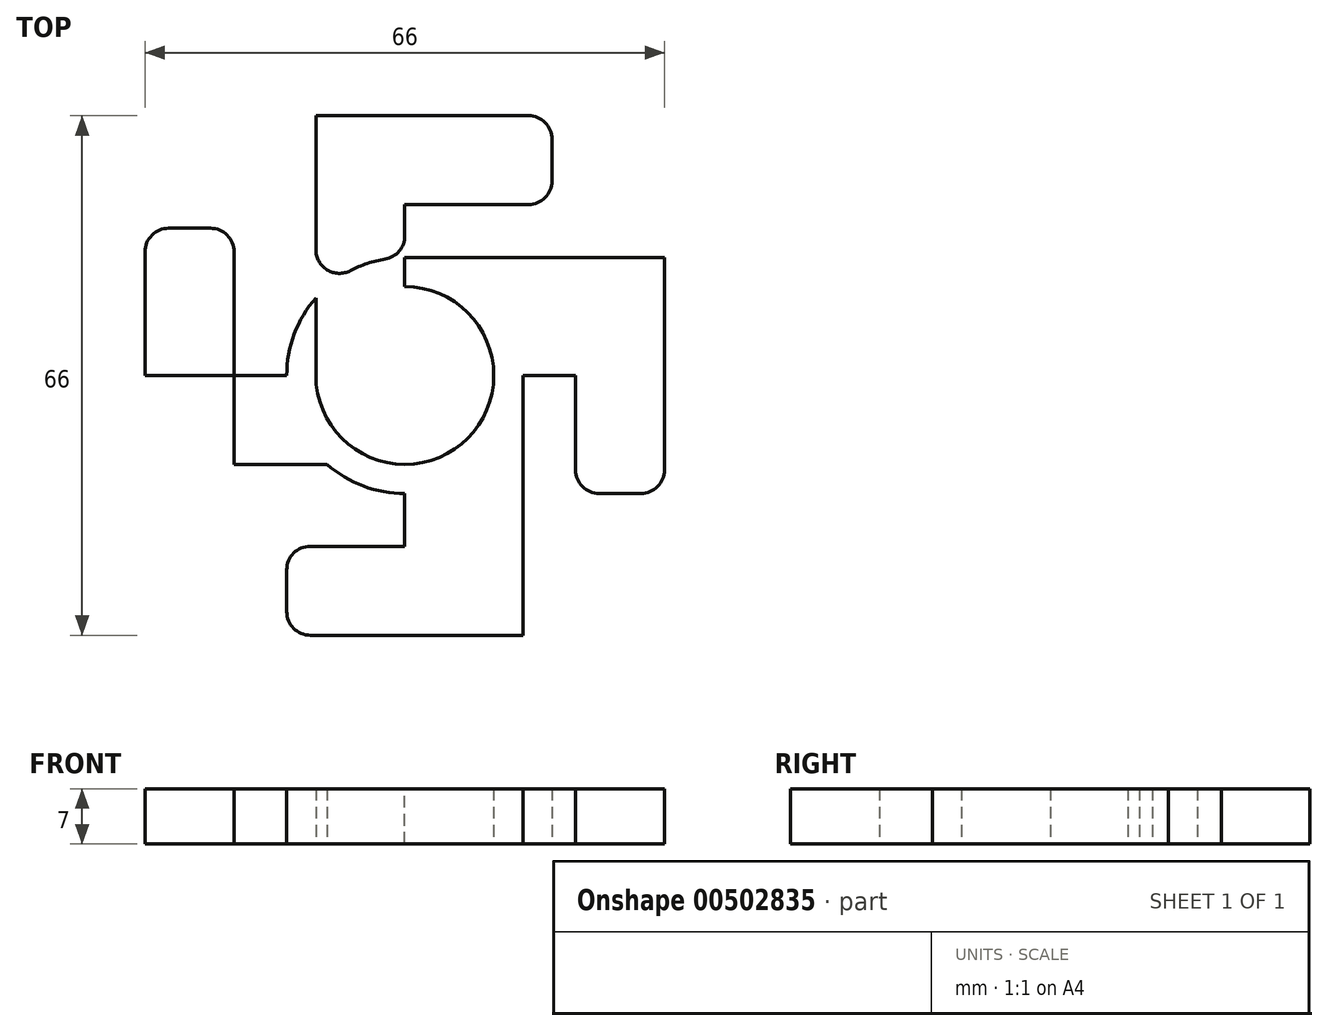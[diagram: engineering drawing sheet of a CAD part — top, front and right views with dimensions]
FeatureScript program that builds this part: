
annotation { "Feature Type Name" : "Feature", "Feature Type Description" : "" }
export const myFeature = defineFeature(function(context is Context, id is Id, definition is map)
    precondition{}
    {
        {
            var Q0;
            Q0=qCreatedBy(makeId("Top.planeOp"),FACE);
            var sketch = newSketch(context, id + "F0", { "sketchPlane" : qUnion([Q0])});
            skCircle(sketch, "E0", {"center": v(0, 0) * mm, "radius": 11.3 * mm});
            skLineSegment(sketch, "E1.bottom", {"start": v(0, 0) * mm, "end": v(33, 0) * mm});
            skLineSegment(sketch, "E1.top", {"start": v(0, 15) * mm, "end": v(33, 15) * mm});
            skLineSegment(sketch, "E1.left", {"start": v(0, 0) * mm, "end": v(0, 15) * mm});
            skLineSegment(sketch, "E1.right", {"start": v(33, 0) * mm, "end": v(33, 15) * mm});
            skLineSegment(sketch, "E2.bottom", {"start": v(33, 15) * mm, "end": v(21.7, 15) * mm});
            skLineSegment(sketch, "E2.top", {"start": v(33, -15) * mm, "end": v(21.7, -15) * mm});
            skLineSegment(sketch, "E2.left", {"start": v(33, 15) * mm, "end": v(33, -15) * mm});
            skLineSegment(sketch, "E2.right", {"start": v(21.7, 15) * mm, "end": v(21.7, -15) * mm});
            skLineSegment(sketch, "E3.bottom", {"start": v(0, 0) * mm, "end": v(15, 0) * mm});
            skLineSegment(sketch, "E3.top", {"start": v(0, -33) * mm, "end": v(15, -33) * mm});
            skLineSegment(sketch, "E3.left", {"start": v(0, 0) * mm, "end": v(0, -33) * mm});
            skLineSegment(sketch, "E3.right", {"start": v(15, 0) * mm, "end": v(15, -33) * mm});
            skLineSegment(sketch, "E4.bottom", {"start": v(15, -33) * mm, "end": v(-15, -33) * mm});
            skLineSegment(sketch, "E4.top", {"start": v(15, -21.7) * mm, "end": v(-15, -21.7) * mm});
            skLineSegment(sketch, "E4.left", {"start": v(15, -33) * mm, "end": v(15, -21.7) * mm});
            skLineSegment(sketch, "E4.right", {"start": v(-15, -33) * mm, "end": v(-15, -21.7) * mm});
            skLineSegment(sketch, "E5.bottom", {"start": v(0, 0) * mm, "end": v(-33, 0) * mm});
            skLineSegment(sketch, "E5.top", {"start": v(0, -11.3) * mm, "end": v(-33, -11.3) * mm});
            skLineSegment(sketch, "E5.left", {"start": v(0, 0) * mm, "end": v(0, -11.3) * mm});
            skLineSegment(sketch, "E5.right", {"start": v(-33, 0) * mm, "end": v(-33, -11.3) * mm});
            skLineSegment(sketch, "E6.bottom", {"start": v(-33, -11.3) * mm, "end": v(-21.7, -11.3) * mm});
            skLineSegment(sketch, "E6.top", {"start": v(-33, 18.7) * mm, "end": v(-21.7, 18.7) * mm});
            skLineSegment(sketch, "E6.left", {"start": v(-33, -11.3) * mm, "end": v(-33, 18.7) * mm});
            skLineSegment(sketch, "E6.right", {"start": v(-21.7, -11.3) * mm, "end": v(-21.7, 18.7) * mm});
            skLineSegment(sketch, "E7.bottom", {"start": v(0, 0) * mm, "end": v(-11.3, 0) * mm});
            skLineSegment(sketch, "E7.top", {"start": v(0, 33) * mm, "end": v(-11.3, 33) * mm});
            skLineSegment(sketch, "E7.left", {"start": v(0, 0) * mm, "end": v(0, 33) * mm});
            skLineSegment(sketch, "E7.right", {"start": v(-11.3, 0) * mm, "end": v(-11.3, 33) * mm});
            skLineSegment(sketch, "E8.bottom", {"start": v(-11.3, 33) * mm, "end": v(18.7, 33) * mm});
            skLineSegment(sketch, "E8.top", {"start": v(-11.3, 21.7) * mm, "end": v(18.7, 21.7) * mm});
            skLineSegment(sketch, "E8.left", {"start": v(-11.3, 33) * mm, "end": v(-11.3, 21.7) * mm});
            skLineSegment(sketch, "E8.right", {"start": v(18.7, 33) * mm, "end": v(18.7, 21.7) * mm});
            skCircle(sketch, "E9", {"center": v(0, 0) * mm, "radius": 15 * mm});
            skSolve(sketch);
        }
        {
            var Q0;
            {var subQ1=sQuery(id+"F0.wireOp",EDGE,"E0");var subQ3=sQuery(id+"F0.wireOp",EDGE,"E7.left");var subQ4=makeQuery(id+"F0.imprint","INTERSECT",VERTEX,{"derivedFrom":[subQ1,subQ3]});Q0=makeQuery(id+"F0.imprint","IMPRINT",FACE,{"disambiguationData":[TD([[makeQuery(id+"F0.imprint","IMPRINT",EDGE,{"disambiguationData":[TD([[subQ4,-1.0]])],"derivedFrom":subQ3}),1.0]])]});}
            var Q1;
            {var subQ1=sQuery(id+"F0.wireOp",EDGE,"E5.bottom");var subQ3=sQuery(id+"F0.wireOp",EDGE,"E9");var subQ4=makeQuery(id+"F0.imprint","INTERSECT",VERTEX,{"derivedFrom":[subQ1,subQ3]});Q1=makeQuery(id+"F0.imprint","IMPRINT",FACE,{"disambiguationData":[TD([[makeQuery(id+"F0.imprint","IMPRINT",EDGE,{"disambiguationData":[TD([[subQ4,1.0]])],"derivedFrom":subQ3}),1.0]])]});}
            var Q2;
            {var subQ3=sQuery(id+"F0.wireOp",EDGE,"E5.bottom");var subQ5=sQuery(id+"F0.wireOp",EDGE,"E9");var subQ6=makeQuery(id+"F0.imprint","INTERSECT",VERTEX,{"derivedFrom":[subQ3,subQ5]});Q2=makeQuery(id+"F0.imprint","IMPRINT",FACE,{"disambiguationData":[TD([[makeQuery(id+"F0.imprint","IMPRINT",EDGE,{"disambiguationData":[TD([[subQ6,-1.0]])],"derivedFrom":subQ5}),1.0]])]});}
            var Q3;
            {var subQ0=sQuery(id+"F0.wireOp",EDGE,"E9");var subQ1=sQuery(id+"F0.wireOp",EDGE,"E5.bottom");var subQ2=makeQuery(id+"F0.imprint","INTERSECT",VERTEX,{"derivedFrom":[subQ1,subQ0]});Q3=makeQuery(id+"F0.imprint","IMPRINT",FACE,{"disambiguationData":[TD([[makeQuery(id+"F0.imprint","IMPRINT",EDGE,{"disambiguationData":[TD([[subQ2,-1.0]])],"derivedFrom":subQ1}),1.0]])]});}
            var Q4;
            {var subQ5=sQuery(id+"F0.wireOp",EDGE,"E6.bottom");Q4=makeQuery(id+"F0.imprint","IMPRINT",FACE,{"disambiguationData":[TD([[makeQuery(id+"F0.imprint","IMPRINT",EDGE,{"derivedFrom":subQ5}),1.0]])]});}
            var Q5;
            {var subQ5=sQuery(id+"F0.wireOp",EDGE,"E6.top");Q5=makeQuery(id+"F0.imprint","IMPRINT",FACE,{"disambiguationData":[TD([[makeQuery(id+"F0.imprint","IMPRINT",EDGE,{"derivedFrom":subQ5}),-1.0]])]});}
            var Q6;
            {var subQ1=sQuery(id+"F0.wireOp",EDGE,"E7.left");var subQ3=sQuery(id+"F0.wireOp",EDGE,"E8.top");var subQ4=makeQuery(id+"F0.imprint","INTERSECT",VERTEX,{"derivedFrom":[subQ1,subQ3]});Q6=makeQuery(id+"F0.imprint","IMPRINT",FACE,{"disambiguationData":[TD([[makeQuery(id+"F0.imprint","IMPRINT",EDGE,{"disambiguationData":[TD([[subQ4,1.0]])],"derivedFrom":subQ1}),1.0]])]});}
            var Q7;
            {var subQ5=sQuery(id+"F0.wireOp",EDGE,"E8.left");Q7=makeQuery(id+"F0.imprint","IMPRINT",FACE,{"disambiguationData":[TD([[makeQuery(id+"F0.imprint","IMPRINT",EDGE,{"derivedFrom":subQ5}),1.0]])]});}
            var Q8;
            {var subQ5=sQuery(id+"F0.wireOp",EDGE,"E8.right");Q8=makeQuery(id+"F0.imprint","IMPRINT",FACE,{"disambiguationData":[TD([[makeQuery(id+"F0.imprint","IMPRINT",EDGE,{"derivedFrom":subQ5}),-1.0]])]});}
            var Q9;
            {var subQ5=sQuery(id+"F0.wireOp",EDGE,"E1.top");Q9=makeQuery(id+"F0.imprint","IMPRINT",FACE,{"disambiguationData":[TD([[makeQuery(id+"F0.imprint","IMPRINT",EDGE,{"derivedFrom":subQ5}),-1.0]])]});}
            var Q10;
            {var subQ5=sQuery(id+"F0.wireOp",EDGE,"E2.bottom");Q10=makeQuery(id+"F0.imprint","IMPRINT",FACE,{"disambiguationData":[TD([[makeQuery(id+"F0.imprint","IMPRINT",EDGE,{"derivedFrom":subQ5}),1.0]])]});}
            var Q11;
            {var subQ5=sQuery(id+"F0.wireOp",EDGE,"E2.top");Q11=makeQuery(id+"F0.imprint","IMPRINT",FACE,{"disambiguationData":[TD([[makeQuery(id+"F0.imprint","IMPRINT",EDGE,{"derivedFrom":subQ5}),-1.0]])]});}
            var Q12;
            {var subQ5=sQuery(id+"F0.wireOp",EDGE,"E3.right");Q12=makeQuery(id+"F0.imprint","IMPRINT",FACE,{"disambiguationData":[TD([[makeQuery(id+"F0.imprint","IMPRINT",EDGE,{"derivedFrom":subQ5}),-1.0]])]});}
            var Q13;
            {var subQ5=sQuery(id+"F0.wireOp",EDGE,"E4.left");Q13=makeQuery(id+"F0.imprint","IMPRINT",FACE,{"disambiguationData":[TD([[makeQuery(id+"F0.imprint","IMPRINT",EDGE,{"derivedFrom":subQ5}),1.0]])]});}
            var Q14;
            {var subQ5=sQuery(id+"F0.wireOp",EDGE,"E4.right");Q14=makeQuery(id+"F0.imprint","IMPRINT",FACE,{"disambiguationData":[TD([[makeQuery(id+"F0.imprint","IMPRINT",EDGE,{"derivedFrom":subQ5}),-1.0]])]});}
            var Q15;
            {var subQ1=sQuery(id+"F0.wireOp",EDGE,"E0");var subQ3=sQuery(id+"F0.wireOp",EDGE,"E3.bottom");var subQ4=makeQuery(id+"F0.imprint","INTERSECT",VERTEX,{"derivedFrom":[subQ1,subQ3]});Q15=makeQuery(id+"F0.imprint","IMPRINT",FACE,{"disambiguationData":[TD([[makeQuery(id+"F0.imprint","IMPRINT",EDGE,{"disambiguationData":[TD([[subQ4,1.0]])],"derivedFrom":subQ1}),-1.0]])]});}
            var Q16;
            {var subQ1=sQuery(id+"F0.wireOp",EDGE,"E3.left");var subQ3=sQuery(id+"F0.wireOp",EDGE,"E9");var subQ4=makeQuery(id+"F0.imprint","INTERSECT",VERTEX,{"derivedFrom":[subQ1,subQ3]});Q16=makeQuery(id+"F0.imprint","IMPRINT",FACE,{"disambiguationData":[TD([[makeQuery(id+"F0.imprint","IMPRINT",EDGE,{"disambiguationData":[TD([[subQ4,1.0]])],"derivedFrom":subQ3}),1.0]])]});}
            var Q17;
            {var subQ0=sQuery(id+"F0.wireOp",EDGE,"E7.left");var subQ1=sQuery(id+"F0.wireOp",EDGE,"E0");var subQ2=makeQuery(id+"F0.imprint","INTERSECT",VERTEX,{"derivedFrom":[subQ1,subQ0]});Q17=makeQuery(id+"F0.imprint","IMPRINT",FACE,{"disambiguationData":[TD([[makeQuery(id+"F0.imprint","IMPRINT",EDGE,{"disambiguationData":[TD([[subQ2,1.0]])],"derivedFrom":subQ1}),-1.0]])]});}
            extrude(context, id + "F1", {"entities" : qUnion([Q0, Q1, Q2, Q3, Q4, Q5, Q6, Q7, Q8, Q9, Q10, Q11, Q12, Q13, Q14, Q15, Q16, Q17]), "depth" : 7 * mm});
        }
        {
            var Q0;
            Q0=makeQuery(id+"F1.opExtrude","SWEPT_EDGE",EDGE,{"disambiguationData":[OSD([sQuery(id+"F0.wireOp",EDGE,"E1.bottom"),sQuery(id+"F0.wireOp",EDGE,"E2.right")])]});
            var Q1;
            Q1=makeQuery(id+"F1.opExtrude","SWEPT_EDGE",EDGE,{"disambiguationData":[OSD([sQuery(id+"F0.wireOp",EDGE,"E3.left"),sQuery(id+"F0.wireOp",EDGE,"E4.top")])]});
            var Q2;
            Q2=makeQuery(id+"F1.opExtrude","SWEPT_EDGE",EDGE,{"disambiguationData":[OSD([sQuery(id+"F0.wireOp",EDGE,"E5.bottom"),sQuery(id+"F0.wireOp",EDGE,"E9")])]});
            var Q3;
            Q3=makeQuery(id+"F1.opExtrude","SWEPT_EDGE",EDGE,{"disambiguationData":[OSD([sQuery(id+"F0.wireOp",EDGE,"E1.top"),sQuery(id+"F0.wireOp",EDGE,"E7.left"),sQuery(id+"F0.wireOp",EDGE,"E9")])]});
            var Q4;
            Q4=makeQuery(id+"F1.opExtrude","SWEPT_EDGE",EDGE,{"disambiguationData":[OSD([sQuery(id+"F0.wireOp",EDGE,"E7.right"),sQuery(id+"F0.wireOp",EDGE,"E9")])]});
            var Q5;
            Q5=makeQuery(id+"F1.opExtrude","SWEPT_EDGE",EDGE,{"disambiguationData":[OSD([sQuery(id+"F0.wireOp",EDGE,"E3.left"),sQuery(id+"F0.wireOp",EDGE,"E9")])]});
            var Q6;
            Q6=makeQuery(id+"F1.opExtrude","SWEPT_EDGE",EDGE,{"disambiguationData":[OSD([sQuery(id+"F0.wireOp",EDGE,"E5.top"),sQuery(id+"F0.wireOp",EDGE,"E9")])]});
            var Q7;
            Q7=makeQuery(id+"F1.opExtrude","SWEPT_EDGE",EDGE,{"disambiguationData":[OSD([sQuery(id+"F0.wireOp",EDGE,"E1.bottom"),sQuery(id+"F0.wireOp",EDGE,"E3.bottom"),sQuery(id+"F0.wireOp",EDGE,"E3.right"),sQuery(id+"F0.wireOp",EDGE,"E9")])]});
            fillet(context, id + "F2", {"entities" : qUnion([Q0, Q1, Q2, Q3, Q4, Q5, Q6, Q7]), "radius" : 3 * mm, "tangentPropagation" : true, "allowEdgeOverflow" : false});
        }
        {
            var Q0;
            Q0=makeQuery(id+"F1.opExtrude","SWEPT_EDGE",EDGE,{"disambiguationData":[OSD([sQuery(id+"F0.wireOp",EDGE,"E6.bottom"),sQuery(id+"F0.wireOp",EDGE,"E6.left")])]});
            var Q1;
            Q1=makeQuery(id+"F1.opExtrude","SWEPT_EDGE",EDGE,{"disambiguationData":[OSD([sQuery(id+"F0.wireOp",EDGE,"E4.bottom"),sQuery(id+"F0.wireOp",EDGE,"E4.right")])]});
            var Q2;
            Q2=makeQuery(id+"F1.opExtrude","SWEPT_EDGE",EDGE,{"disambiguationData":[OSD([sQuery(id+"F0.wireOp",EDGE,"E6.top"),sQuery(id+"F0.wireOp",EDGE,"E6.left")])]});
            var Q3;
            Q3=makeQuery(id+"F1.opExtrude","SWEPT_EDGE",EDGE,{"disambiguationData":[OSD([sQuery(id+"F0.wireOp",EDGE,"E6.top"),sQuery(id+"F0.wireOp",EDGE,"E6.right")])]});
            var Q4;
            Q4=makeQuery(id+"F1.opExtrude","SWEPT_EDGE",EDGE,{"disambiguationData":[OSD([sQuery(id+"F0.wireOp",EDGE,"E4.top"),sQuery(id+"F0.wireOp",EDGE,"E4.right")])]});
            var Q5;
            Q5=makeQuery(id+"F1.opExtrude","SWEPT_EDGE",EDGE,{"disambiguationData":[OSD([sQuery(id+"F0.wireOp",EDGE,"E4.bottom"),sQuery(id+"F0.wireOp",EDGE,"E4.left")])]});
            var Q6;
            Q6=makeQuery(id+"F1.opExtrude","SWEPT_EDGE",EDGE,{"disambiguationData":[OSD([sQuery(id+"F0.wireOp",EDGE,"E2.top"),sQuery(id+"F0.wireOp",EDGE,"E2.right")])]});
            var Q7;
            Q7=makeQuery(id+"F1.opExtrude","SWEPT_EDGE",EDGE,{"disambiguationData":[OSD([sQuery(id+"F0.wireOp",EDGE,"E2.top"),sQuery(id+"F0.wireOp",EDGE,"E2.left")])]});
            var Q8;
            Q8=makeQuery(id+"F1.opExtrude","SWEPT_EDGE",EDGE,{"disambiguationData":[OSD([sQuery(id+"F0.wireOp",EDGE,"E2.bottom"),sQuery(id+"F0.wireOp",EDGE,"E2.left")])]});
            var Q9;
            Q9=makeQuery(id+"F1.opExtrude","SWEPT_EDGE",EDGE,{"disambiguationData":[OSD([sQuery(id+"F0.wireOp",EDGE,"E8.top"),sQuery(id+"F0.wireOp",EDGE,"E8.right")])]});
            var Q10;
            Q10=makeQuery(id+"F1.opExtrude","SWEPT_EDGE",EDGE,{"disambiguationData":[OSD([sQuery(id+"F0.wireOp",EDGE,"E8.bottom"),sQuery(id+"F0.wireOp",EDGE,"E8.right")])]});
            var Q11;
            Q11=makeQuery(id+"F1.opExtrude","SWEPT_EDGE",EDGE,{"disambiguationData":[OSD([sQuery(id+"F0.wireOp",EDGE,"E8.bottom"),sQuery(id+"F0.wireOp",EDGE,"E8.left")])]});
            fillet(context, id + "F3", {"entities" : qUnion([Q0, Q1, Q2, Q3, Q4, Q5, Q6, Q7, Q8, Q9, Q10, Q11]), "radius" : 3 * mm, "tangentPropagation" : true, "allowEdgeOverflow" : false});
        }
    });
